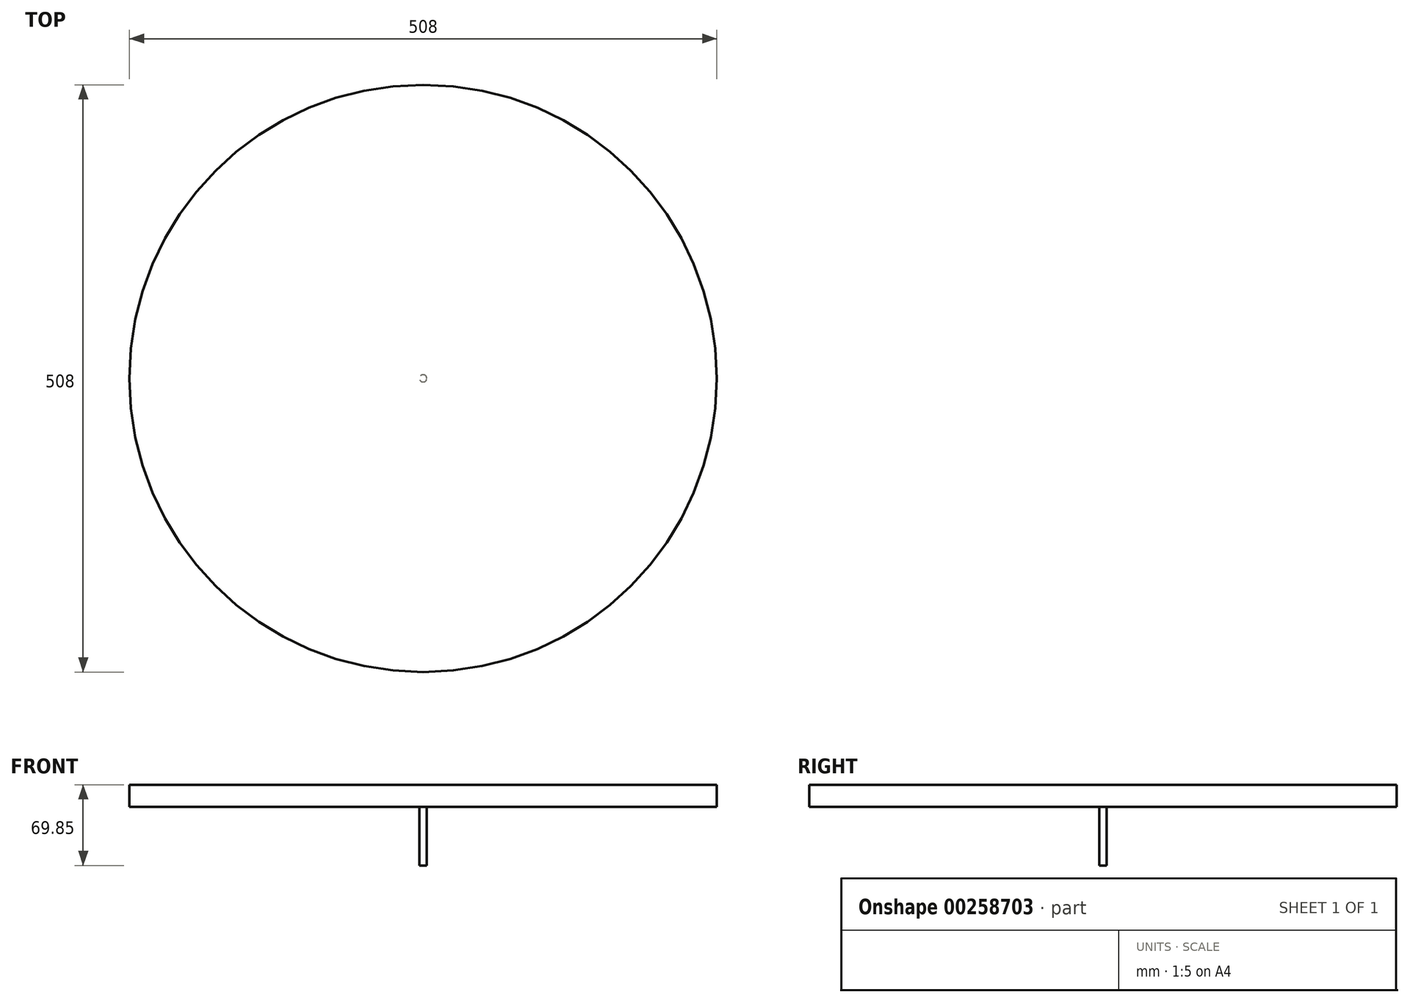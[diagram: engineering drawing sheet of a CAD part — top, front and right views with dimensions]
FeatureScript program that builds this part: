
annotation { "Feature Type Name" : "Feature", "Feature Type Description" : "" }
export const myFeature = defineFeature(function(context is Context, id is Id, definition is map)
    precondition{}
    {
        {
            var Q0;
            Q0=qCreatedBy(makeId("Top.planeOp"),FACE);
            var sketch = newSketch(context, id + "F0", { "sketchPlane" : qUnion([Q0])});
            skCircle(sketch, "E0", {"center": v(0, 0) * mm, "radius": 254 * mm});
            skSolve(sketch);
        }
        {
            var Q0;
            Q0 = qSketchRegion(id + "F0", true);
            extrude(context, id + "F1", {"entities" : qUnion([Q0]), "depth" : 19.05 * mm});
        }
        {
            var Q0;
            Q0=makeQuery(id+"F1.opExtrude","CAP_FACE",FACE,{"disambiguationData":[OSD([sQuery(id+"F0.wireOp",EDGE,"E0")])],"isStart":true});
            var sketch = newSketch(context, id + "F2", { "sketchPlane" : qUnion([Q0])});
            skCircle(sketch, "E1", {"center": v(0, 0) * mm, "radius": 3.18 * mm});
            skSolve(sketch);
        }
        {
            var Q0;
            Q0 = qSketchRegion(id + "F2", true);
            extrude(context, id + "F3", {"entities" : qUnion([Q0]), "depth" : 50.8 * mm});
        }
        {
            var Q0;
            Q0=qCreatedBy(makeId("Top.planeOp"),FACE);
            cPlane(context, id + "F4", {"entities" : qUnion([Q0]), "cplaneType" : CPlaneType.OFFSET, "offset" : 38.1 * mm, "oppositeDirection" : true, "width" : 152.4 * mm, "height" : 152.4 * mm});
        }
    });
